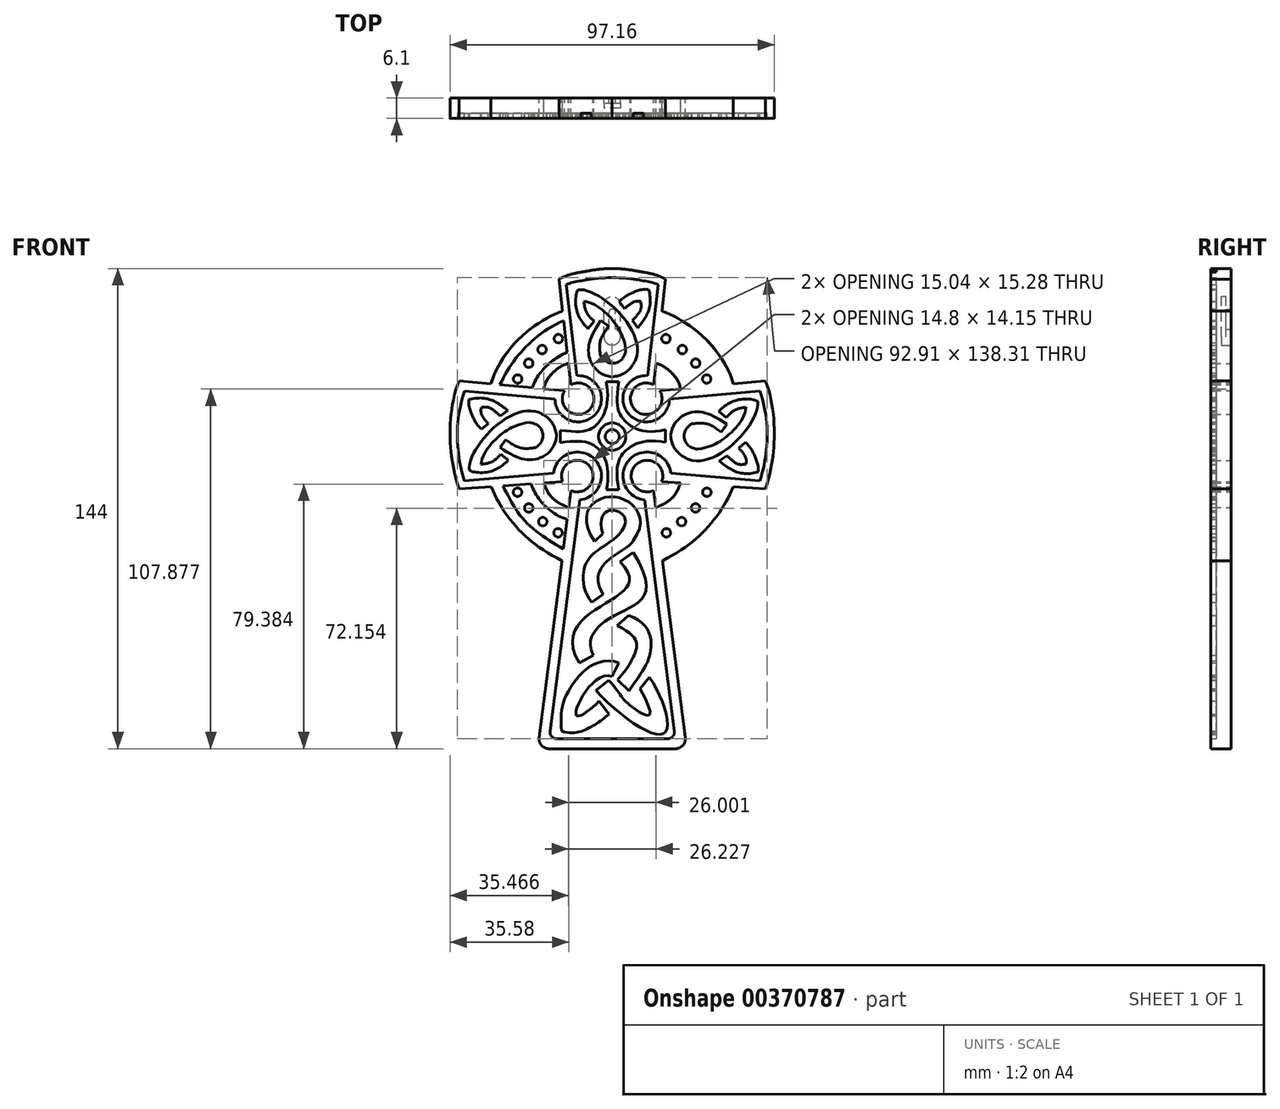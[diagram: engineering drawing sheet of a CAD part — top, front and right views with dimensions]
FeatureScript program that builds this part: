
annotation { "Feature Type Name" : "Feature", "Feature Type Description" : "" }
export const myFeature = defineFeature(function(context is Context, id is Id, definition is map)
    precondition{}
    {
        {
            var Q0;
            Q0=qCreatedBy(makeId("Front.planeOp"),FACE);
            var sketch = newSketch(context, id + "F0", { "sketchPlane" : qUnion([Q0])});
            skLineSegment(sketch, "E0", {"start": v(-15.98, 47.24) * mm, "end": v(-12.37, 15.55) * mm});
            skFitSpline(sketch, "E1", {"points": [v(-15.98, 47.24) * mm, v(-8.08, 49.54) * mm, v(0, 50.37) * mm], "startDerivative": vector(18.02, 9.08) * mm, "endDerivative": vector(16.55, -0.59) * mm});
            skFitSpline(sketch, "E2", {"points": [v(-36.31, 15.75) * mm, v(-28.77, 28.48) * mm, v(-14.9, 37.7) * mm], "startDerivative": vector(4.28, 18.82) * mm, "endDerivative": vector(22.42, 8.54) * mm});
            skLineSegment(sketch, "E3", {"start": v(-45.93, 16.65) * mm, "end": v(-14.25, 13.78) * mm});
            skFitSpline(sketch, "E4", {"points": [v(-45.93, 16.65) * mm, v(-48.57, 0) * mm, v(-45.93, -15.65) * mm], "startDerivative": vector(-12.44, -31.32) * mm, "endDerivative": vector(11.03, -33.67) * mm});
            skLineSegment(sketch, "E5", {"start": v(-45.93, -15.65) * mm, "end": v(-14.86, -13.53) * mm});
            skFitSpline(sketch, "E6", {"points": [v(-20.52, 14.34) * mm, v(-17.86, 19.03) * mm, v(-13.1, 21.9) * mm], "startDerivative": vector(2.95, 13.03) * mm, "endDerivative": vector(12.02, 1.87) * mm});
            skLineSegment(sketch, "E7", {"start": v(-12.37, -16.17) * mm, "end": v(-21.9, -90.24) * mm});
            skFitSpline(sketch, "E8", {"points": [v(-36.23, -14.99) * mm, v(-28.9, -26.9) * mm, v(-15.08, -37.22) * mm], "startDerivative": vector(9.94, -26.4) * mm, "endDerivative": vector(36.07, -18.64) * mm});
            skFitSpline(sketch, "E9", {"points": [v(-20.51, -13.91) * mm, v(-18.02, -18.35) * mm, v(-13.03, -21.31) * mm], "startDerivative": vector(3.98, -10.28) * mm, "endDerivative": vector(10.53, -4.43) * mm});
            skLineSegment(sketch, "E10", {"start": v(-18.92, -93.62) * mm, "end": v(0, -93.62) * mm});
            skArc(sketch, "E11", {"start": v(-14.25, 13.78) * mm, "mid": v(-6.95, 7.9) * mm, "end": v(-12.37, 15.55) * mm});
            skArc(sketch, "E12", {"start": v(-12.37, -16.17) * mm, "mid": v(-6.99, -8.6) * mm, "end": v(-14.86, -13.53) * mm});
            skPoint(sketch, "E13.visualSharp", {"position": v(-22.33, -93.62) * mm});
            skArc(sketch, "E13.filletArc", {"start": v(-21.9, -90.24) * mm, "mid": v(-21.18, -92.6) * mm, "end": v(-18.92, -93.62) * mm});
            skFitSpline(sketch, "E14.MirrorCS", {"points": [v(15.98, 47.24) * mm, v(8.08, 49.54) * mm, v(0, 50.37) * mm], "startDerivative": vector(-18.02, 9.08) * mm, "endDerivative": vector(-16.55, -0.59) * mm});
            skLineSegment(sketch, "E15.MirrorCS", {"start": v(15.98, 47.24) * mm, "end": v(12.37, 15.55) * mm});
            skFitSpline(sketch, "E16.MirrorCS", {"points": [v(36.31, 15.75) * mm, v(28.77, 28.48) * mm, v(14.9, 37.7) * mm], "startDerivative": vector(-4.28, 18.82) * mm, "endDerivative": vector(-22.42, 8.54) * mm});
            skFitSpline(sketch, "E17.MirrorCS", {"points": [v(20.52, 14.34) * mm, v(17.86, 19.03) * mm, v(13.1, 21.9) * mm], "startDerivative": vector(-2.95, 13.03) * mm, "endDerivative": vector(-12.02, 1.87) * mm});
            skLineSegment(sketch, "E18.MirrorCS", {"start": v(45.93, 16.65) * mm, "end": v(14.25, 13.78) * mm});
            skArc(sketch, "E19.MirrorCS", {"start": v(14.25, 13.78) * mm, "mid": v(6.95, 7.9) * mm, "end": v(12.37, 15.55) * mm});
            skFitSpline(sketch, "E20.MirrorCS", {"points": [v(45.93, 16.65) * mm, v(48.57, 0) * mm, v(45.93, -15.65) * mm], "startDerivative": vector(12.44, -31.32) * mm, "endDerivative": vector(-11.03, -33.67) * mm});
            skLineSegment(sketch, "E21.MirrorCS", {"start": v(45.93, -15.65) * mm, "end": v(14.86, -13.53) * mm});
            skArc(sketch, "E22.MirrorCS", {"start": v(12.37, -16.17) * mm, "mid": v(6.99, -8.6) * mm, "end": v(14.86, -13.53) * mm});
            skFitSpline(sketch, "E23.MirrorCS", {"points": [v(20.51, -13.91) * mm, v(18.02, -18.35) * mm, v(13.03, -21.31) * mm], "startDerivative": vector(-3.98, -10.28) * mm, "endDerivative": vector(-10.53, -4.43) * mm});
            skFitSpline(sketch, "E24.MirrorCS", {"points": [v(36.23, -14.99) * mm, v(28.9, -26.9) * mm, v(15.08, -37.22) * mm], "startDerivative": vector(-9.94, -26.4) * mm, "endDerivative": vector(-36.07, -18.64) * mm});
            skLineSegment(sketch, "E25.MirrorCS", {"start": v(12.37, -16.17) * mm, "end": v(21.9, -90.24) * mm});
            skArc(sketch, "E26.MirrorCS", {"start": v(21.9, -90.24) * mm, "mid": v(21.18, -92.6) * mm, "end": v(18.92, -93.62) * mm});
            skLineSegment(sketch, "E27.MirrorCS", {"start": v(18.92, -93.62) * mm, "end": v(0, -93.62) * mm});
            skSolve(sketch);
        }
        {
            var Q0;
            Q0 = qSketchRegion(id + "F0", true);
            extrude(context, id + "F1", {"entities" : qUnion([Q0]), "depth" : 4.5 * mm});
        }
        {
            var Q0;
            Q0=makeQuery(id+"F1.opExtrude","CAP_FACE",FACE,{"disambiguationData":[OSD([sQuery(id+"F0.wireOp",EDGE,"E0"),sQuery(id+"F0.wireOp",EDGE,"E1"),sQuery(id+"F0.wireOp",EDGE,"E2"),sQuery(id+"F0.wireOp",EDGE,"E3"),sQuery(id+"F0.wireOp",EDGE,"E4"),sQuery(id+"F0.wireOp",EDGE,"E5"),sQuery(id+"F0.wireOp",EDGE,"E6"),sQuery(id+"F0.wireOp",EDGE,"E7"),sQuery(id+"F0.wireOp",EDGE,"E8"),sQuery(id+"F0.wireOp",EDGE,"E9"),sQuery(id+"F0.wireOp",EDGE,"E10"),sQuery(id+"F0.wireOp",EDGE,"E11"),sQuery(id+"F0.wireOp",EDGE,"E12"),sQuery(id+"F0.wireOp",EDGE,"E13.filletArc"),sQuery(id+"F0.wireOp",EDGE,"E14.MirrorCS"),sQuery(id+"F0.wireOp",EDGE,"E15.MirrorCS"),sQuery(id+"F0.wireOp",EDGE,"E16.MirrorCS"),sQuery(id+"F0.wireOp",EDGE,"E17.MirrorCS"),sQuery(id+"F0.wireOp",EDGE,"E18.MirrorCS"),sQuery(id+"F0.wireOp",EDGE,"E19.MirrorCS"),sQuery(id+"F0.wireOp",EDGE,"E20.MirrorCS"),sQuery(id+"F0.wireOp",EDGE,"E21.MirrorCS"),sQuery(id+"F0.wireOp",EDGE,"E22.MirrorCS"),sQuery(id+"F0.wireOp",EDGE,"E23.MirrorCS"),sQuery(id+"F0.wireOp",EDGE,"E24.MirrorCS"),sQuery(id+"F0.wireOp",EDGE,"E25.MirrorCS"),sQuery(id+"F0.wireOp",EDGE,"E26.MirrorCS"),sQuery(id+"F0.wireOp",EDGE,"E27.MirrorCS")])],"isStart":false});
            var sketch = newSketch(context, id + "F2", { "sketchPlane" : qUnion([Q0])});
            skLineSegment(sketch, "E28", {"start": v(-15.98, 47.24) * mm, "end": v(-12.37, 15.55) * mm});
            skFitSpline(sketch, "E29", {"points": [v(-13.74, 45.58) * mm, v(-7.87, 46.97) * mm, v(0, 47.69) * mm], "startDerivative": vector(10.43, 4.57) * mm, "endDerivative": vector(27.81, 0.9) * mm});
            skLineSegment(sketch, "E30", {"start": v(-13.74, 45.58) * mm, "end": v(-10.63, 18.29) * mm});
            skLineSegment(sketch, "E31", {"start": v(-45.93, 16.65) * mm, "end": v(-14.25, 13.78) * mm});
            skLineSegment(sketch, "E32", {"start": v(-44.25, 13.64) * mm, "end": v(-17.14, 11.18) * mm});
            skLineSegment(sketch, "E33", {"start": v(-45.93, -15.65) * mm, "end": v(-14.86, -13.53) * mm});
            skLineSegment(sketch, "E34", {"start": v(-44.33, -13.3) * mm, "end": v(-17.59, -11.01) * mm});
            skFitSpline(sketch, "E35", {"points": [v(-44.25, 13.64) * mm, v(-46.45, 0) * mm, v(-44.33, -13.3) * mm], "startDerivative": vector(-9.37, -27.38) * mm, "endDerivative": vector(7.76, -27.9) * mm});
            skFitSpline(sketch, "E36", {"points": [v(-33.66, 15.54) * mm, v(-26.53, 26.22) * mm, v(-14.56, 34.76) * mm], "startDerivative": vector(12.12, 25.5) * mm, "endDerivative": vector(28.6, 12.19) * mm});
            skFitSpline(sketch, "E37", {"points": [v(-23.92, 14.65) * mm, v(-20.1, 20.75) * mm, v(-13.48, 25.31) * mm], "startDerivative": vector(5.37, 16.36) * mm, "endDerivative": vector(16.27, 7.08) * mm});
            skFitSpline(sketch, "E38", {"points": [v(-20.52, 14.34) * mm, v(-17.75, 19.15) * mm, v(-13.1, 21.9) * mm], "startDerivative": vector(3.12, 14.47) * mm, "endDerivative": vector(12.63, 2.18) * mm});
            skLineSegment(sketch, "E39", {"start": v(-12.37, -16.17) * mm, "end": v(-21.9, -90.24) * mm});
            skLineSegment(sketch, "E40", {"start": v(-9.71, -19.02) * mm, "end": v(-18.63, -88.37) * mm});
            skLineSegment(sketch, "E41", {"start": v(-16.65, -90.62) * mm, "end": v(0, -90.62) * mm});
            skLineSegment(sketch, "E42", {"start": v(-18.92, -93.62) * mm, "end": v(0, -93.62) * mm});
            skPoint(sketch, "E43.visualSharp", {"position": v(-22.33, -93.62) * mm});
            skArc(sketch, "E43.filletArc", {"start": v(-21.9, -90.24) * mm, "mid": v(-21.18, -92.6) * mm, "end": v(-18.92, -93.62) * mm});
            skArc(sketch, "E44.filletArc", {"start": v(-18.63, -88.37) * mm, "mid": v(-18.15, -89.94) * mm, "end": v(-16.65, -90.62) * mm});
            skFitSpline(sketch, "E45", {"points": [v(-20.51, -13.91) * mm, v(-17.84, -18.52) * mm, v(-13.03, -21.31) * mm], "startDerivative": vector(4.43, -10.23) * mm, "endDerivative": vector(10.52, -4.59) * mm});
            skFitSpline(sketch, "E46", {"points": [v(-24.29, -14.17) * mm, v(-20.04, -20.86) * mm, v(-13.48, -24.8) * mm], "startDerivative": vector(5.22, -16.41) * mm, "endDerivative": vector(16.74, -4.5) * mm});
            skFitSpline(sketch, "E47", {"points": [v(-32.74, -14.75) * mm, v(-26.14, -25.32) * mm, v(-14.63, -33.74) * mm], "startDerivative": vector(11.58, -23.24) * mm, "endDerivative": vector(24.5, -14.84) * mm});
            skArc(sketch, "E48", {"start": v(-17.14, 11.18) * mm, "mid": v(-5.07, 6.65) * mm, "end": v(-10.63, 18.29) * mm});
            skArc(sketch, "E49", {"start": v(-14.25, 13.78) * mm, "mid": v(-6.95, 7.9) * mm, "end": v(-12.37, 15.55) * mm});
            skArc(sketch, "E50", {"start": v(-9.71, -19.02) * mm, "mid": v(-5.3, -6.8) * mm, "end": v(-17.59, -11.01) * mm});
            skArc(sketch, "E51", {"start": v(-12.37, -16.17) * mm, "mid": v(-6.99, -8.6) * mm, "end": v(-14.86, -13.53) * mm});
            skCircle(sketch, "E52", {"center": v(-16.12, 29.36) * mm, "radius": 1.27 * mm});
            skCircle(sketch, "E53", {"center": v(-21.02, 26.1) * mm, "radius": 1.27 * mm});
            skCircle(sketch, "E54", {"center": v(-25.02, 22) * mm, "radius": 1.27 * mm});
            skCircle(sketch, "E55", {"center": v(-28.32, 17.27) * mm, "radius": 1.27 * mm});
            skCircle(sketch, "E56", {"center": v(-28.36, -16.7) * mm, "radius": 1.27 * mm});
            skCircle(sketch, "E57", {"center": v(-25, -21.4) * mm, "radius": 1.27 * mm});
            skCircle(sketch, "E58", {"center": v(-20.8, -25.52) * mm, "radius": 1.27 * mm});
            skCircle(sketch, "E59", {"center": v(-16.23, -28.86) * mm, "radius": 1.27 * mm});
            skCircle(sketch, "E60.MirrorC", {"center": v(25.02, 22) * mm, "radius": 1.27 * mm});
            skCircle(sketch, "E61.MirrorC", {"center": v(28.32, 17.27) * mm, "radius": 1.27 * mm});
            skFitSpline(sketch, "E62.MirrorCS", {"points": [v(20.51, -13.91) * mm, v(17.84, -18.52) * mm, v(13.03, -21.31) * mm], "startDerivative": vector(-4.43, -10.23) * mm, "endDerivative": vector(-10.52, -4.59) * mm});
            skCircle(sketch, "E63.MirrorC", {"center": v(25, -21.4) * mm, "radius": 1.27 * mm});
            skArc(sketch, "E64.MirrorCS", {"start": v(18.63, -88.37) * mm, "mid": v(18.15, -89.94) * mm, "end": v(16.65, -90.62) * mm});
            skCircle(sketch, "E65.MirrorC", {"center": v(28.36, -16.7) * mm, "radius": 1.27 * mm});
            skCircle(sketch, "E66.MirrorC", {"center": v(21.02, 26.1) * mm, "radius": 1.27 * mm});
            skCircle(sketch, "E67.MirrorC", {"center": v(16.12, 29.36) * mm, "radius": 1.27 * mm});
            skFitSpline(sketch, "E68.MirrorCS", {"points": [v(24.29, -14.17) * mm, v(20.04, -20.86) * mm, v(13.48, -24.8) * mm], "startDerivative": vector(-5.22, -16.41) * mm, "endDerivative": vector(-16.74, -4.5) * mm});
            skCircle(sketch, "E69.MirrorC", {"center": v(16.23, -28.86) * mm, "radius": 1.27 * mm});
            skFitSpline(sketch, "E70.MirrorCS", {"points": [v(23.92, 14.65) * mm, v(20.1, 20.75) * mm, v(13.48, 25.31) * mm], "startDerivative": vector(-5.37, 16.36) * mm, "endDerivative": vector(-16.27, 7.08) * mm});
            skCircle(sketch, "E71.MirrorC", {"center": v(20.8, -25.52) * mm, "radius": 1.27 * mm});
            skFitSpline(sketch, "E72.MirrorCS", {"points": [v(20.52, 14.34) * mm, v(17.75, 19.15) * mm, v(13.1, 21.9) * mm], "startDerivative": vector(-3.12, 14.47) * mm, "endDerivative": vector(-12.63, 2.18) * mm});
            skFitSpline(sketch, "E73.MirrorCS", {"points": [v(13.74, 45.58) * mm, v(7.87, 46.97) * mm, v(0, 47.69) * mm], "startDerivative": vector(-10.43, 4.57) * mm, "endDerivative": vector(-27.81, 0.9) * mm});
            skArc(sketch, "E74.MirrorCS", {"start": v(21.9, -90.24) * mm, "mid": v(21.18, -92.6) * mm, "end": v(18.92, -93.62) * mm});
            skArc(sketch, "E75.MirrorCS", {"start": v(12.37, -16.17) * mm, "mid": v(6.99, -8.6) * mm, "end": v(14.86, -13.53) * mm});
            skArc(sketch, "E76.MirrorCS", {"start": v(17.14, 11.18) * mm, "mid": v(5.07, 6.65) * mm, "end": v(10.63, 18.29) * mm});
            skLineSegment(sketch, "E77.MirrorCS", {"start": v(18.92, -93.62) * mm, "end": v(0, -93.62) * mm});
            skLineSegment(sketch, "E78.MirrorCS", {"start": v(16.65, -90.62) * mm, "end": v(0, -90.62) * mm});
            skFitSpline(sketch, "E79.MirrorCS", {"points": [v(32.74, -14.75) * mm, v(26.14, -25.32) * mm, v(14.63, -33.74) * mm], "startDerivative": vector(-11.58, -23.24) * mm, "endDerivative": vector(-24.5, -14.84) * mm});
            skArc(sketch, "E80.MirrorCS", {"start": v(9.71, -19.02) * mm, "mid": v(5.3, -6.8) * mm, "end": v(17.59, -11.01) * mm});
            skArc(sketch, "E81.MirrorCS", {"start": v(14.25, 13.78) * mm, "mid": v(6.95, 7.9) * mm, "end": v(12.37, 15.55) * mm});
            skFitSpline(sketch, "E82.MirrorCS", {"points": [v(33.66, 15.54) * mm, v(26.53, 26.22) * mm, v(14.56, 34.76) * mm], "startDerivative": vector(-12.12, 25.5) * mm, "endDerivative": vector(-28.6, 12.19) * mm});
            skLineSegment(sketch, "E83.MirrorCS", {"start": v(15.98, 47.24) * mm, "end": v(12.37, 15.55) * mm});
            skLineSegment(sketch, "E84.MirrorCS", {"start": v(13.74, 45.58) * mm, "end": v(10.63, 18.29) * mm});
            skLineSegment(sketch, "E85.MirrorCS", {"start": v(9.71, -19.02) * mm, "end": v(18.63, -88.37) * mm});
            skFitSpline(sketch, "E86.MirrorCS", {"points": [v(44.25, 13.64) * mm, v(46.45, 0) * mm, v(44.33, -13.3) * mm], "startDerivative": vector(9.37, -27.38) * mm, "endDerivative": vector(-7.76, -27.9) * mm});
            skLineSegment(sketch, "E87.MirrorCS", {"start": v(44.33, -13.3) * mm, "end": v(17.59, -11.01) * mm});
            skPoint(sketch, "E88.MirrorP", {"position": v(22.33, -93.62) * mm});
            skLineSegment(sketch, "E89.MirrorCS", {"start": v(12.37, -16.17) * mm, "end": v(21.9, -90.24) * mm});
            skLineSegment(sketch, "E90.MirrorCS", {"start": v(44.25, 13.64) * mm, "end": v(17.14, 11.18) * mm});
            skLineSegment(sketch, "E91.MirrorCS", {"start": v(45.93, -15.65) * mm, "end": v(14.86, -13.53) * mm});
            skLineSegment(sketch, "E92.MirrorCS", {"start": v(45.93, 16.65) * mm, "end": v(14.25, 13.78) * mm});
            skFitSpline(sketch, "E93.0", {"points": [v(-15.98, 47.24) * mm, v(-12.97, 48.76) * mm, v(-8.33, 49.46) * mm, v(-2.75, 50.47) * mm, v(0, 50.37) * mm]});
            skFitSpline(sketch, "E94.0", {"points": [v(-36.31, 15.75) * mm, v(-35.62, 18.8) * mm, v(-29.86, 29.97) * mm, v(-18.74, 36.23) * mm, v(-14.9, 37.7) * mm]});
            skFitSpline(sketch, "E95.0", {"points": [v(-45.93, 16.65) * mm, v(-48.03, 11.35) * mm, v(-49.26, -0.3) * mm, v(-47.74, -10.12) * mm, v(-45.93, -15.65) * mm]});
            skFitSpline(sketch, "E96.0", {"points": [v(-36.23, -14.99) * mm, v(-34.66, -19.16) * mm, v(-29.06, -28.02) * mm, v(-21.4, -33.95) * mm, v(-15.08, -37.22) * mm]});
            skFitSpline(sketch, "E97.MirrorCS", {"points": [v(15.98, 47.24) * mm, v(12.97, 48.76) * mm, v(8.33, 49.46) * mm, v(2.75, 50.47) * mm, v(0, 50.37) * mm]});
            skFitSpline(sketch, "E98.MirrorCS", {"points": [v(36.31, 15.75) * mm, v(35.62, 18.8) * mm, v(29.86, 29.97) * mm, v(18.74, 36.23) * mm, v(14.9, 37.7) * mm]});
            skFitSpline(sketch, "E99.MirrorCS", {"points": [v(45.93, 16.65) * mm, v(48.03, 11.35) * mm, v(49.26, -0.3) * mm, v(47.74, -10.12) * mm, v(45.93, -15.65) * mm]});
            skFitSpline(sketch, "E100.MirrorCS", {"points": [v(36.23, -14.99) * mm, v(34.66, -19.16) * mm, v(29.06, -28.02) * mm, v(21.4, -33.95) * mm, v(15.08, -37.22) * mm]});
            skSolve(sketch);
        }
        {
            var Q0;
            Q0=makeQuery(id+"F2.imprint","IMPRINT",FACE,{"disambiguationData":[TD([[makeQuery(id+"F2.imprint","IMPRINT",EDGE,{"derivedFrom":sQuery(id+"F2.wireOp",EDGE,"E29")}),1.0]])]});
            var Q1;
            {var subQ3=sQuery(id+"F2.wireOp",EDGE,"E36");Q1=makeQuery(id+"F2.imprint","IMPRINT",FACE,{"disambiguationData":[TD([[makeQuery(id+"F2.imprint","IMPRINT",EDGE,{"derivedFrom":subQ3}),1.0]])]});}
            var Q2;
            {var subQ5=sQuery(id+"F2.wireOp",EDGE,"E37");Q2=makeQuery(id+"F2.imprint","IMPRINT",FACE,{"disambiguationData":[TD([[makeQuery(id+"F2.imprint","IMPRINT",EDGE,{"derivedFrom":subQ5}),-1.0]])]});}
            var Q3;
            {var subQ0=sQuery(id+"F2.wireOp",EDGE,"E82.MirrorCS");Q3=makeQuery(id+"F2.imprint","IMPRINT",FACE,{"disambiguationData":[TD([[makeQuery(id+"F2.imprint","IMPRINT",EDGE,{"derivedFrom":subQ0}),-1.0]])]});}
            var Q4;
            {var subQ4=sQuery(id+"F2.wireOp",EDGE,"E68.MirrorCS");Q4=makeQuery(id+"F2.imprint","IMPRINT",FACE,{"disambiguationData":[TD([[makeQuery(id+"F2.imprint","IMPRINT",EDGE,{"derivedFrom":subQ4}),-1.0]])]});}
            var Q5;
            {var subQ0=sQuery(id+"F2.wireOp",EDGE,"E79.MirrorCS");Q5=makeQuery(id+"F2.imprint","IMPRINT",FACE,{"disambiguationData":[TD([[makeQuery(id+"F2.imprint","IMPRINT",EDGE,{"derivedFrom":subQ0}),1.0]])]});}
            var Q6;
            {var subQ0=sQuery(id+"F2.wireOp",EDGE,"E46");Q6=makeQuery(id+"F2.imprint","IMPRINT",FACE,{"disambiguationData":[TD([[makeQuery(id+"F2.imprint","IMPRINT",EDGE,{"derivedFrom":subQ0}),1.0]])]});}
            var Q7;
            {var subQ2=sQuery(id+"F2.wireOp",EDGE,"E47");Q7=makeQuery(id+"F2.imprint","IMPRINT",FACE,{"disambiguationData":[TD([[makeQuery(id+"F2.imprint","IMPRINT",EDGE,{"derivedFrom":subQ2}),-1.0]])]});}
            var Q8;
            Q8=makeQuery(id+"F2.imprint","IMPRINT",FACE,{"disambiguationData":[TD([[makeQuery(id+"F2.imprint","IMPRINT",EDGE,{"derivedFrom":sQuery(id+"F2.wireOp",EDGE,"E56")}),1.0]])]});
            var Q9;
            Q9=makeQuery(id+"F2.imprint","IMPRINT",FACE,{"disambiguationData":[TD([[makeQuery(id+"F2.imprint","IMPRINT",EDGE,{"derivedFrom":sQuery(id+"F2.wireOp",EDGE,"E57")}),1.0]])]});
            var Q10;
            Q10=makeQuery(id+"F2.imprint","IMPRINT",FACE,{"disambiguationData":[TD([[makeQuery(id+"F2.imprint","IMPRINT",EDGE,{"derivedFrom":sQuery(id+"F2.wireOp",EDGE,"E59")}),1.0]])]});
            var Q11;
            Q11=makeQuery(id+"F2.imprint","IMPRINT",FACE,{"disambiguationData":[TD([[makeQuery(id+"F2.imprint","IMPRINT",EDGE,{"derivedFrom":sQuery(id+"F2.wireOp",EDGE,"E58")}),1.0]])]});
            var Q12;
            Q12=makeQuery(id+"F2.imprint","IMPRINT",FACE,{"disambiguationData":[TD([[makeQuery(id+"F2.imprint","IMPRINT",EDGE,{"derivedFrom":sQuery(id+"F2.wireOp",EDGE,"E65.MirrorC")}),-1.0]])]});
            var Q13;
            Q13=makeQuery(id+"F2.imprint","IMPRINT",FACE,{"disambiguationData":[TD([[makeQuery(id+"F2.imprint","IMPRINT",EDGE,{"derivedFrom":sQuery(id+"F2.wireOp",EDGE,"E63.MirrorC")}),-1.0]])]});
            var Q14;
            Q14=makeQuery(id+"F2.imprint","IMPRINT",FACE,{"disambiguationData":[TD([[makeQuery(id+"F2.imprint","IMPRINT",EDGE,{"derivedFrom":sQuery(id+"F2.wireOp",EDGE,"E71.MirrorC")}),-1.0]])]});
            var Q15;
            Q15=makeQuery(id+"F2.imprint","IMPRINT",FACE,{"disambiguationData":[TD([[makeQuery(id+"F2.imprint","IMPRINT",EDGE,{"derivedFrom":sQuery(id+"F2.wireOp",EDGE,"E69.MirrorC")}),-1.0]])]});
            var Q16;
            Q16=makeQuery(id+"F2.imprint","IMPRINT",FACE,{"disambiguationData":[TD([[makeQuery(id+"F2.imprint","IMPRINT",EDGE,{"derivedFrom":sQuery(id+"F2.wireOp",EDGE,"E67.MirrorC")}),-1.0]])]});
            var Q17;
            Q17=makeQuery(id+"F2.imprint","IMPRINT",FACE,{"disambiguationData":[TD([[makeQuery(id+"F2.imprint","IMPRINT",EDGE,{"derivedFrom":sQuery(id+"F2.wireOp",EDGE,"E66.MirrorC")}),-1.0]])]});
            var Q18;
            Q18=makeQuery(id+"F2.imprint","IMPRINT",FACE,{"disambiguationData":[TD([[makeQuery(id+"F2.imprint","IMPRINT",EDGE,{"derivedFrom":sQuery(id+"F2.wireOp",EDGE,"E60.MirrorC")}),-1.0]])]});
            var Q19;
            Q19=makeQuery(id+"F2.imprint","IMPRINT",FACE,{"disambiguationData":[TD([[makeQuery(id+"F2.imprint","IMPRINT",EDGE,{"derivedFrom":sQuery(id+"F2.wireOp",EDGE,"E61.MirrorC")}),-1.0]])]});
            var Q20;
            {var subQ4=sQuery(id+"F2.wireOp",EDGE,"E70.MirrorCS");Q20=makeQuery(id+"F2.imprint","IMPRINT",FACE,{"disambiguationData":[TD([[makeQuery(id+"F2.imprint","IMPRINT",EDGE,{"derivedFrom":subQ4}),1.0]])]});}
            var Q21;
            Q21=makeQuery(id+"F2.imprint","IMPRINT",FACE,{"disambiguationData":[TD([[makeQuery(id+"F2.imprint","IMPRINT",EDGE,{"derivedFrom":sQuery(id+"F2.wireOp",EDGE,"E52")}),1.0]])]});
            var Q22;
            Q22=makeQuery(id+"F2.imprint","IMPRINT",FACE,{"disambiguationData":[TD([[makeQuery(id+"F2.imprint","IMPRINT",EDGE,{"derivedFrom":sQuery(id+"F2.wireOp",EDGE,"E53")}),1.0]])]});
            var Q23;
            Q23=makeQuery(id+"F2.imprint","IMPRINT",FACE,{"disambiguationData":[TD([[makeQuery(id+"F2.imprint","IMPRINT",EDGE,{"derivedFrom":sQuery(id+"F2.wireOp",EDGE,"E54")}),1.0]])]});
            var Q24;
            Q24=makeQuery(id+"F2.imprint","IMPRINT",FACE,{"disambiguationData":[TD([[makeQuery(id+"F2.imprint","IMPRINT",EDGE,{"derivedFrom":sQuery(id+"F2.wireOp",EDGE,"E55")}),1.0]])]});
            extrude(context, id + "F3", {"entities" : qUnion([Q0, Q1, Q2, Q3, Q4, Q5, Q6, Q7, Q8, Q9, Q10, Q11, Q12, Q13, Q14, Q15, Q16, Q17, Q18, Q19, Q20, Q21, Q22, Q23, Q24]), "operationType" : NewBodyOperationType.ADD, "depth" : 1.6 * mm});
        }
        {
            var Q0;
            Q0=makeQuery(id+"F3.boolean.opBoolean","SPLIT",FACE,{"disambiguationData":[TD([makeQuery(id+"F3.opExtrude","SWEPT_FACE",FACE,{"disambiguationData":[OSD([sQuery(id+"F2.wireOp",EDGE,"E29")])]})])],"derivedFrom":makeQuery(id+"F1.opExtrude","CAP_FACE",FACE,{"disambiguationData":[OSD([sQuery(id+"F0.wireOp",EDGE,"E0"),sQuery(id+"F0.wireOp",EDGE,"E1"),sQuery(id+"F0.wireOp",EDGE,"E2"),sQuery(id+"F0.wireOp",EDGE,"E3"),sQuery(id+"F0.wireOp",EDGE,"E4"),sQuery(id+"F0.wireOp",EDGE,"E5"),sQuery(id+"F0.wireOp",EDGE,"E6"),sQuery(id+"F0.wireOp",EDGE,"E7"),sQuery(id+"F0.wireOp",EDGE,"E8"),sQuery(id+"F0.wireOp",EDGE,"E9"),sQuery(id+"F0.wireOp",EDGE,"E10"),sQuery(id+"F0.wireOp",EDGE,"E11"),sQuery(id+"F0.wireOp",EDGE,"E12"),sQuery(id+"F0.wireOp",EDGE,"E13.filletArc"),sQuery(id+"F0.wireOp",EDGE,"E14.MirrorCS"),sQuery(id+"F0.wireOp",EDGE,"E15.MirrorCS"),sQuery(id+"F0.wireOp",EDGE,"E16.MirrorCS"),sQuery(id+"F0.wireOp",EDGE,"E17.MirrorCS"),sQuery(id+"F0.wireOp",EDGE,"E18.MirrorCS"),sQuery(id+"F0.wireOp",EDGE,"E19.MirrorCS"),sQuery(id+"F0.wireOp",EDGE,"E20.MirrorCS"),sQuery(id+"F0.wireOp",EDGE,"E21.MirrorCS"),sQuery(id+"F0.wireOp",EDGE,"E22.MirrorCS"),sQuery(id+"F0.wireOp",EDGE,"E23.MirrorCS"),sQuery(id+"F0.wireOp",EDGE,"E24.MirrorCS"),sQuery(id+"F0.wireOp",EDGE,"E25.MirrorCS"),sQuery(id+"F0.wireOp",EDGE,"E26.MirrorCS"),sQuery(id+"F0.wireOp",EDGE,"E27.MirrorCS")])],"isStart":false})});
            var sketch = newSketch(context, id + "F4", { "sketchPlane" : qUnion([Q0])});
            skFitSpline(sketch, "E101", {"points": [v(-10.27, 44.05) * mm, v(1.63, 37.59) * mm, v(7.12, 23.2) * mm], "startDerivative": vector(19.44, 2.29) * mm, "endDerivative": vector(-9.65, -26.54) * mm});
            skFitSpline(sketch, "E102", {"points": [v(-10.27, 44.05) * mm, v(-10.77, 38.37) * mm, v(-7.27, 32.33) * mm], "startDerivative": vector(-4.28, -6.57) * mm, "endDerivative": vector(10.2, -10.74) * mm});
            skLineSegment(sketch, "E103", {"start": v(-7.27, 32.33) * mm, "end": v(-5.42, 34.64) * mm});
            skFitSpline(sketch, "E104", {"points": [v(-5.42, 34.64) * mm, v(-7.6, 37.04) * mm, v(-8.51, 40.5) * mm], "startDerivative": vector(-5.1, 4.48) * mm, "endDerivative": vector(-1.12, 7.21) * mm});
            skFitSpline(sketch, "E105", {"points": [v(-8.51, 40.5) * mm, v(0, 35.05) * mm, v(4.08, 26.15) * mm], "startDerivative": vector(18.67, -0.82) * mm, "endDerivative": vector(3.63, -23.43) * mm});
            skFitSpline(sketch, "E106", {"points": [v(-3.53, 24.35) * mm, v(0.62, 22) * mm, v(4.08, 26.15) * mm], "startDerivative": vector(5.11, -10.51) * mm, "endDerivative": vector(1.62, 15.64) * mm});
            skFitSpline(sketch, "E107", {"points": [v(-3.44, 34.82) * mm, v(-7, 24.35) * mm, v(0, 17.9) * mm], "startDerivative": vector(-16.54, -24.8) * mm, "endDerivative": vector(26.33, -2.87) * mm});
            skLineSegment(sketch, "E108", {"start": v(-3.44, 34.82) * mm, "end": v(-1.09, 33.12) * mm});
            skFitSpline(sketch, "E109", {"points": [v(-1.09, 33.12) * mm, v(-3.53, 28.74) * mm, v(-3.53, 24.35) * mm], "startDerivative": vector(-5.95, -8.32) * mm, "endDerivative": vector(1.14, -9.21) * mm});
            skFitSpline(sketch, "E110", {"points": [v(0, 17.9) * mm, v(4.68, 19.74) * mm, v(7.12, 23.2) * mm], "startDerivative": vector(11.25, 1.33) * mm, "endDerivative": vector(4.18, 8.1) * mm});
            skFitSpline(sketch, "E111", {"points": [v(2.07, 40.39) * mm, v(5.9, 43.03) * mm, v(10.9, 44.16) * mm], "startDerivative": vector(9.87, 10.5) * mm, "endDerivative": vector(13.91, -0.9) * mm});
            skLineSegment(sketch, "E112", {"start": v(2.07, 40.39) * mm, "end": v(3.72, 38.32) * mm});
            skFitSpline(sketch, "E113", {"points": [v(3.72, 38.32) * mm, v(5.84, 40.03) * mm, v(8.58, 40.44) * mm], "startDerivative": vector(3.96, 4.08) * mm, "endDerivative": vector(7.1, -2.16) * mm});
            skFitSpline(sketch, "E114", {"points": [v(8.58, 40.44) * mm, v(8.11, 37.29) * mm, v(6.05, 34.8) * mm], "startDerivative": vector(1.51, -10.58) * mm, "endDerivative": vector(-4.27, -4.3) * mm});
            skLineSegment(sketch, "E115", {"start": v(6.05, 34.8) * mm, "end": v(7.65, 32.53) * mm});
            skFitSpline(sketch, "E116", {"points": [v(10.9, 44.16) * mm, v(10.9, 37.75) * mm, v(7.65, 32.53) * mm], "startDerivative": vector(4, -14.43) * mm, "endDerivative": vector(-8.2, -10.02) * mm});
            skFitSpline(sketch, "E117", {"points": [v(43.63, 10.56) * mm, v(37.18, -1.34) * mm, v(22.79, -6.83) * mm], "startDerivative": vector(2.29, -19.44) * mm, "endDerivative": vector(-26.54, 9.65) * mm});
            skFitSpline(sketch, "E118", {"points": [v(43.63, 10.56) * mm, v(37.96, 11.06) * mm, v(31.92, 7.56) * mm], "startDerivative": vector(-6.57, 4.28) * mm, "endDerivative": vector(-10.74, -10.2) * mm});
            skLineSegment(sketch, "E119", {"start": v(31.92, 7.56) * mm, "end": v(34.23, 5.72) * mm});
            skFitSpline(sketch, "E120", {"points": [v(34.23, 5.72) * mm, v(36.62, 7.88) * mm, v(40.08, 8.8) * mm], "startDerivative": vector(4.48, 5.1) * mm, "endDerivative": vector(7.21, 1.12) * mm});
            skFitSpline(sketch, "E121", {"points": [v(40.08, 8.8) * mm, v(34.64, 0.3) * mm, v(25.74, -3.78) * mm], "startDerivative": vector(-0.82, -18.67) * mm, "endDerivative": vector(-23.43, -3.63) * mm});
            skFitSpline(sketch, "E122", {"points": [v(23.94, 3.82) * mm, v(21.59, -0.33) * mm, v(25.74, -3.78) * mm], "startDerivative": vector(-10.51, -5.11) * mm, "endDerivative": vector(15.64, -1.62) * mm});
            skFitSpline(sketch, "E123", {"points": [v(34.4, 3.73) * mm, v(23.94, 7.28) * mm, v(17.49, 0.3) * mm], "startDerivative": vector(-24.8, 16.54) * mm, "endDerivative": vector(-2.87, -26.33) * mm});
            skLineSegment(sketch, "E124", {"start": v(34.4, 3.73) * mm, "end": v(32.7, 1.38) * mm});
            skFitSpline(sketch, "E125", {"points": [v(32.7, 1.38) * mm, v(28.32, 3.82) * mm, v(23.94, 3.82) * mm], "startDerivative": vector(-8.32, 5.95) * mm, "endDerivative": vector(-9.21, -1.14) * mm});
            skFitSpline(sketch, "E126", {"points": [v(17.49, 0.3) * mm, v(19.33, -4.38) * mm, v(22.79, -6.83) * mm], "startDerivative": vector(1.33, -11.25) * mm, "endDerivative": vector(8.1, -4.18) * mm});
            skFitSpline(sketch, "E127", {"points": [v(39.98, -1.77) * mm, v(42.61, -5.6) * mm, v(43.75, -10.61) * mm], "startDerivative": vector(10.5, -9.87) * mm, "endDerivative": vector(-0.9, -13.91) * mm});
            skLineSegment(sketch, "E128", {"start": v(39.98, -1.77) * mm, "end": v(37.9, -3.43) * mm});
            skFitSpline(sketch, "E129", {"points": [v(37.9, -3.43) * mm, v(39.61, -5.55) * mm, v(40.03, -8.29) * mm], "startDerivative": vector(4.08, -3.96) * mm, "endDerivative": vector(-2.16, -7.1) * mm});
            skFitSpline(sketch, "E130", {"points": [v(40.03, -8.29) * mm, v(36.87, -7.82) * mm, v(34.4, -5.75) * mm], "startDerivative": vector(-10.58, -1.51) * mm, "endDerivative": vector(-4.3, 4.27) * mm});
            skLineSegment(sketch, "E131", {"start": v(34.4, -5.75) * mm, "end": v(32.12, -7.36) * mm});
            skFitSpline(sketch, "E132", {"points": [v(43.75, -10.61) * mm, v(37.34, -10.61) * mm, v(32.12, -7.36) * mm], "startDerivative": vector(-14.43, -4) * mm, "endDerivative": vector(-10.02, 8.2) * mm});
            skFitSpline(sketch, "E133", {"points": [v(-42.83, -10.1) * mm, v(-36.37, 1.8) * mm, v(-21.99, 7.28) * mm], "startDerivative": vector(-2.29, 19.44) * mm, "endDerivative": vector(26.54, -9.65) * mm});
            skFitSpline(sketch, "E134", {"points": [v(-42.83, -10.1) * mm, v(-37.16, -10.6) * mm, v(-31.12, -7.1) * mm], "startDerivative": vector(6.57, -4.28) * mm, "endDerivative": vector(10.74, 10.2) * mm});
            skLineSegment(sketch, "E135", {"start": v(-31.12, -7.1) * mm, "end": v(-33.42, -5.26) * mm});
            skFitSpline(sketch, "E136", {"points": [v(-33.42, -5.26) * mm, v(-35.82, -7.43) * mm, v(-39.28, -8.35) * mm], "startDerivative": vector(-4.48, -5.1) * mm, "endDerivative": vector(-7.21, -1.12) * mm});
            skFitSpline(sketch, "E137", {"points": [v(-39.28, -8.35) * mm, v(-33.84, 0.16) * mm, v(-24.94, 4.24) * mm], "startDerivative": vector(0.82, 18.67) * mm, "endDerivative": vector(23.43, 3.63) * mm});
            skFitSpline(sketch, "E138", {"points": [v(-23.14, -3.37) * mm, v(-20.79, 0.78) * mm, v(-24.94, 4.24) * mm], "startDerivative": vector(10.51, 5.11) * mm, "endDerivative": vector(-15.64, 1.62) * mm});
            skFitSpline(sketch, "E139", {"points": [v(-33.6, -3.28) * mm, v(-23.14, -6.83) * mm, v(-16.68, 0.16) * mm], "startDerivative": vector(24.8, -16.54) * mm, "endDerivative": vector(2.87, 26.33) * mm});
            skLineSegment(sketch, "E140", {"start": v(-33.6, -3.28) * mm, "end": v(-31.9, -0.93) * mm});
            skFitSpline(sketch, "E141", {"points": [v(-31.9, -0.93) * mm, v(-27.52, -3.37) * mm, v(-23.14, -3.37) * mm], "startDerivative": vector(8.32, -5.95) * mm, "endDerivative": vector(9.21, 1.14) * mm});
            skFitSpline(sketch, "E142", {"points": [v(-16.68, 0.16) * mm, v(-18.53, 4.84) * mm, v(-21.99, 7.28) * mm], "startDerivative": vector(-1.33, 11.25) * mm, "endDerivative": vector(-8.1, 4.18) * mm});
            skFitSpline(sketch, "E143", {"points": [v(-39.17, 2.23) * mm, v(-41.8, 6.05) * mm, v(-42.95, 11.07) * mm], "startDerivative": vector(-10.5, 9.87) * mm, "endDerivative": vector(0.9, 13.91) * mm});
            skLineSegment(sketch, "E144", {"start": v(-39.17, 2.23) * mm, "end": v(-37.1, 3.88) * mm});
            skFitSpline(sketch, "E145", {"points": [v(-37.1, 3.88) * mm, v(-38.81, 6) * mm, v(-39.23, 8.74) * mm], "startDerivative": vector(-4.08, 3.96) * mm, "endDerivative": vector(2.16, 7.1) * mm});
            skFitSpline(sketch, "E146", {"points": [v(-39.23, 8.74) * mm, v(-36.07, 8.28) * mm, v(-33.6, 6.2) * mm], "startDerivative": vector(10.58, 1.51) * mm, "endDerivative": vector(4.3, -4.27) * mm});
            skLineSegment(sketch, "E147", {"start": v(-33.6, 6.2) * mm, "end": v(-31.32, 7.81) * mm});
            skFitSpline(sketch, "E148", {"points": [v(-42.95, 11.07) * mm, v(-36.54, 11.07) * mm, v(-31.32, 7.81) * mm], "startDerivative": vector(14.43, 4) * mm, "endDerivative": vector(10.02, -8.2) * mm});
            skLineSegment(sketch, "E149", {"start": v(-1.8, 16.45) * mm, "end": v(1.94, 16.45) * mm});
            skLineSegment(sketch, "E150", {"start": v(-15.51, 1.88) * mm, "end": v(-15.51, -1.87) * mm});
            skLineSegment(sketch, "E151", {"start": v(16, 2.07) * mm, "end": v(16, -1.68) * mm});
            skLineSegment(sketch, "E152", {"start": v(-1.74, -15.93) * mm, "end": v(2.01, -15.93) * mm});
            skFitSpline(sketch, "E153", {"points": [v(-15.51, 1.88) * mm, v(-4.1, 4.16) * mm, v(-1.8, 16.45) * mm], "startDerivative": vector(41.53, -6) * mm, "endDerivative": vector(-7.24, 33.18) * mm});
            skFitSpline(sketch, "E154", {"points": [v(-15.51, -1.87) * mm, v(-3.97, -3.85) * mm, v(-1.74, -15.93) * mm], "startDerivative": vector(36.43, 6.33) * mm, "endDerivative": vector(-6.89, -32.53) * mm});
            skFitSpline(sketch, "E155", {"points": [v(1.94, 16.45) * mm, v(3.98, 4.53) * mm, v(16, 2.07) * mm], "startDerivative": vector(-6.7, -43.47) * mm, "endDerivative": vector(38.32, 9.21) * mm});
            skFitSpline(sketch, "E156", {"points": [v(2.01, -15.93) * mm, v(3.92, -4.34) * mm, v(16, -1.68) * mm], "startDerivative": vector(-8.24, 38.97) * mm, "endDerivative": vector(36.87, -6.51) * mm});
            skCircle(sketch, "E157", {"center": v(0, 0) * mm, "radius": 4.09 * mm});
            skCircle(sketch, "E158", {"center": v(0, 0) * mm, "radius": 2.1 * mm});
            skFitSpline(sketch, "E159", {"points": [v(-5.27, -31.46) * mm, v(0, -18.05) * mm, v(6.33, -31.13) * mm], "startDerivative": vector(-34.58, 49.25) * mm, "endDerivative": vector(-32.37, -42.28) * mm});
            skLineSegment(sketch, "E160", {"start": v(-5.27, -31.46) * mm, "end": v(-2.89, -29.18) * mm});
            skLineSegment(sketch, "E161", {"start": v(-6.14, -49.78) * mm, "end": v(-2.74, -47.25) * mm});
            skLineSegment(sketch, "E162", {"start": v(2.4, -37.58) * mm, "end": v(6.33, -34.7) * mm});
            skLineSegment(sketch, "E163", {"start": v(-9.88, -67.91) * mm, "end": v(-5.61, -65.64) * mm});
            skLineSegment(sketch, "E164", {"start": v(1.46, -56.65) * mm, "end": v(4.94, -53.62) * mm});
            skLineSegment(sketch, "E165", {"start": v(0, -71.9) * mm, "end": v(1.98, -67.85) * mm});
            skLineSegment(sketch, "E166", {"start": v(1.57, -72.93) * mm, "end": v(5.1, -76.25) * mm});
            skLineSegment(sketch, "E167", {"start": v(8.3, -75.62) * mm, "end": v(11.1, -72.2) * mm});
            skLineSegment(sketch, "E168", {"start": v(-4.86, -76.14) * mm, "end": v(-1.03, -73.03) * mm});
            skLineSegment(sketch, "E169", {"start": v(-3.93, -79.36) * mm, "end": v(-0.92, -83.2) * mm});
            skFitSpline(sketch, "E170", {"points": [v(-2.74, -47.25) * mm, v(-0.92, -36.85) * mm, v(6.33, -31.13) * mm], "startDerivative": vector(-17.76, 26.07) * mm, "endDerivative": vector(5.76, 12.4) * mm});
            skPoint(sketch, "E171.2.internal.snap0", {"position": v(-4.08, -30.32) * mm});
            skFitSpline(sketch, "E171", {"points": [v(-2.89, -29.18) * mm, v(1.67, -22.45) * mm, v(1.05, -30.32) * mm], "startDerivative": vector(-9.9, 40.84) * mm, "endDerivative": vector(-27, -25.74) * mm});
            skFitSpline(sketch, "E172", {"points": [v(-6.14, -49.78) * mm, v(-7.35, -37.17) * mm, v(1.05, -30.32) * mm], "startDerivative": vector(-19.57, 26.74) * mm, "endDerivative": vector(22.66, 18.13) * mm});
            skFitSpline(sketch, "E173", {"points": [v(2.4, -37.58) * mm, v(0, -48.78) * mm, v(-9.88, -67.91) * mm], "startDerivative": vector(37.41, -39.45) * mm, "endDerivative": vector(32.56, -54.63) * mm});
            skFitSpline(sketch, "E174", {"points": [v(-5.61, -65.64) * mm, v(1.88, -53.03) * mm, v(6.33, -34.7) * mm], "startDerivative": vector(-20.4, 36.98) * mm, "endDerivative": vector(-46.26, 76.55) * mm});
            skFitSpline(sketch, "E175", {"points": [v(1.98, -67.85) * mm, v(-12.64, -75.52) * mm, v(-15.12, -88.27) * mm], "startDerivative": vector(-36.97, 13.5) * mm, "endDerivative": vector(3.97, -31.1) * mm});
            skFitSpline(sketch, "E176", {"points": [v(4.94, -53.62) * mm, v(11.52, -64.43) * mm, v(5.1, -76.25) * mm], "startDerivative": vector(40.1, -13.46) * mm, "endDerivative": vector(-23.9, -35.53) * mm});
            skFitSpline(sketch, "E177", {"points": [v(1.46, -56.65) * mm, v(7.06, -64.22) * mm, v(1.57, -72.93) * mm], "startDerivative": vector(37.54, -18.45) * mm, "endDerivative": vector(-16.42, -17.43) * mm});
            skFitSpline(sketch, "E178", {"points": [v(-1.03, -73.03) * mm, v(6.33, -81.33) * mm, v(8.3, -75.62) * mm], "startDerivative": vector(20, -22.7) * mm, "endDerivative": vector(-46.15, 80.59) * mm});
            skFitSpline(sketch, "E179", {"points": [v(-4.86, -76.14) * mm, v(15.66, -88.9) * mm, v(11.1, -72.2) * mm], "startDerivative": vector(38.47, -42.49) * mm, "endDerivative": vector(-26.46, 37.32) * mm});
            skFitSpline(sketch, "E180", {"points": [v(0, -71.9) * mm, v(-10.87, -83.3) * mm, v(-3.93, -79.36) * mm], "startDerivative": vector(-28.16, 9.05) * mm, "endDerivative": vector(22.43, 21.69) * mm});
            skFitSpline(sketch, "E181", {"points": [v(-15.12, -88.27) * mm, v(-7.04, -87.44) * mm, v(-0.92, -83.2) * mm], "startDerivative": vector(18.26, -6.7) * mm, "endDerivative": vector(11.7, 10.42) * mm});
            skSolve(sketch);
        }
        {
            var Q0;
            Q0 = qSketchRegion(id + "F4", true);
            var Q1;
            Q1=makeQuery(id+"F4.imprint","IMPRINT",FACE,{"disambiguationData":[TD([[makeQuery(id+"F4.imprint","IMPRINT",EDGE,{"derivedFrom":sQuery(id+"F4.wireOp",EDGE,"E158")}),1.0]])]});
            extrude(context, id + "F5", {"entities" : qUnion([Q0, Q1]), "operationType" : NewBodyOperationType.ADD, "depth" : 1.6 * mm});
        }
        {
            var Q0;
            Q0=makeQuery(id+"F1.opExtrude","CAP_FACE",FACE,{"disambiguationData":[OSD([sQuery(id+"F0.wireOp",EDGE,"E0"),sQuery(id+"F0.wireOp",EDGE,"E1"),sQuery(id+"F0.wireOp",EDGE,"E2"),sQuery(id+"F0.wireOp",EDGE,"E3"),sQuery(id+"F0.wireOp",EDGE,"E4"),sQuery(id+"F0.wireOp",EDGE,"E5"),sQuery(id+"F0.wireOp",EDGE,"E6"),sQuery(id+"F0.wireOp",EDGE,"E7"),sQuery(id+"F0.wireOp",EDGE,"E8"),sQuery(id+"F0.wireOp",EDGE,"E9"),sQuery(id+"F0.wireOp",EDGE,"E10"),sQuery(id+"F0.wireOp",EDGE,"E11"),sQuery(id+"F0.wireOp",EDGE,"E12"),sQuery(id+"F0.wireOp",EDGE,"E13.filletArc"),sQuery(id+"F0.wireOp",EDGE,"E14.MirrorCS"),sQuery(id+"F0.wireOp",EDGE,"E15.MirrorCS"),sQuery(id+"F0.wireOp",EDGE,"E16.MirrorCS"),sQuery(id+"F0.wireOp",EDGE,"E17.MirrorCS"),sQuery(id+"F0.wireOp",EDGE,"E18.MirrorCS"),sQuery(id+"F0.wireOp",EDGE,"E19.MirrorCS"),sQuery(id+"F0.wireOp",EDGE,"E20.MirrorCS"),sQuery(id+"F0.wireOp",EDGE,"E21.MirrorCS"),sQuery(id+"F0.wireOp",EDGE,"E22.MirrorCS"),sQuery(id+"F0.wireOp",EDGE,"E23.MirrorCS"),sQuery(id+"F0.wireOp",EDGE,"E24.MirrorCS"),sQuery(id+"F0.wireOp",EDGE,"E25.MirrorCS"),sQuery(id+"F0.wireOp",EDGE,"E26.MirrorCS"),sQuery(id+"F0.wireOp",EDGE,"E27.MirrorCS")])],"isStart":true});
            var sketch = newSketch(context, id + "F6", { "sketchPlane" : qUnion([Q0])});
            skCircle(sketch, "E182", {"center": v(0, 29.93) * mm, "radius": 2.5 * mm});
            skLineSegment(sketch, "E183", {"start": v(-1, 32.22) * mm, "end": v(-1, 37.22) * mm});
            skLineSegment(sketch, "E184", {"start": v(1, 32.22) * mm, "end": v(1, 37.22) * mm});
            skArc(sketch, "E185", {"start": v(-1, 37.22) * mm, "mid": v(0, 38.22) * mm, "end": v(1, 37.22) * mm});
            skSolve(sketch);
        }
        {
            var Q0;
            {var subQ0=sQuery(id+"F6.wireOp",EDGE,"E182");var subQ1=makeQuery(id+"F6.imprint","INTERSECT",VERTEX,{"derivedFrom":[subQ0,sQuery(id+"F6.wireOp",EDGE,"E184")]});Q0=makeQuery(id+"F6.imprint","IMPRINT",FACE,{"disambiguationData":[TD([[makeQuery(id+"F6.imprint","IMPRINT",EDGE,{"disambiguationData":[TD([[subQ1,1.0]])],"derivedFrom":subQ0}),1.0]])]});}
            var Q1;
            {var subQ0=sQuery(id+"F6.wireOp",EDGE,"E183");Q1=makeQuery(id+"F6.imprint","IMPRINT",FACE,{"disambiguationData":[TD([[makeQuery(id+"F6.imprint","IMPRINT",EDGE,{"derivedFrom":subQ0}),-1.0]])]});}
            extrude(context, id + "F7", {"entities" : qUnion([Q0, Q1]), "operationType" : NewBodyOperationType.REMOVE, "oppositeDirection" : true, "depth" : 3 * mm});
        }
        {
            var Q0;
            Q0=makeQuery(id+"F1.opExtrude","CAP_FACE",FACE,{"disambiguationData":[OSD([sQuery(id+"F0.wireOp",EDGE,"E0"),sQuery(id+"F0.wireOp",EDGE,"E1"),sQuery(id+"F0.wireOp",EDGE,"E2"),sQuery(id+"F0.wireOp",EDGE,"E3"),sQuery(id+"F0.wireOp",EDGE,"E4"),sQuery(id+"F0.wireOp",EDGE,"E5"),sQuery(id+"F0.wireOp",EDGE,"E6"),sQuery(id+"F0.wireOp",EDGE,"E7"),sQuery(id+"F0.wireOp",EDGE,"E8"),sQuery(id+"F0.wireOp",EDGE,"E9"),sQuery(id+"F0.wireOp",EDGE,"E10"),sQuery(id+"F0.wireOp",EDGE,"E11"),sQuery(id+"F0.wireOp",EDGE,"E12"),sQuery(id+"F0.wireOp",EDGE,"E13.filletArc"),sQuery(id+"F0.wireOp",EDGE,"E14.MirrorCS"),sQuery(id+"F0.wireOp",EDGE,"E15.MirrorCS"),sQuery(id+"F0.wireOp",EDGE,"E16.MirrorCS"),sQuery(id+"F0.wireOp",EDGE,"E17.MirrorCS"),sQuery(id+"F0.wireOp",EDGE,"E18.MirrorCS"),sQuery(id+"F0.wireOp",EDGE,"E19.MirrorCS"),sQuery(id+"F0.wireOp",EDGE,"E20.MirrorCS"),sQuery(id+"F0.wireOp",EDGE,"E21.MirrorCS"),sQuery(id+"F0.wireOp",EDGE,"E22.MirrorCS"),sQuery(id+"F0.wireOp",EDGE,"E23.MirrorCS"),sQuery(id+"F0.wireOp",EDGE,"E24.MirrorCS"),sQuery(id+"F0.wireOp",EDGE,"E25.MirrorCS"),sQuery(id+"F0.wireOp",EDGE,"E26.MirrorCS"),sQuery(id+"F0.wireOp",EDGE,"E27.MirrorCS")])],"isStart":true});
            cPlane(context, id + "F8", {"entities" : qUnion([Q0]), "cplaneType" : CPlaneType.OFFSET, "offset" : 3 * mm, "oppositeDirection" : true, "width" : 150 * mm, "height" : 150 * mm});
        }
        {
            var Q0;
            Q0=qCreatedBy(id+"F8.planeOp",FACE);
            var sketch = newSketch(context, id + "F9", { "sketchPlane" : qUnion([Q0])});
            skArc(sketch, "E186.0", {"start": v(-2.5, 39.43) * mm, "mid": v(0, 41.93) * mm, "end": v(2.5, 39.43) * mm});
            skLineSegment(sketch, "E187.0", {"start": v(-2.5, 29.93) * mm, "end": v(-2.5, 39.43) * mm});
            skLineSegment(sketch, "E188.0", {"start": v(2.5, 29.93) * mm, "end": v(2.5, 39.43) * mm});
            skLineSegment(sketch, "E189.0", {"start": v(-1, 32.22) * mm, "end": v(-1, 37.22) * mm});
            skArc(sketch, "E189.1", {"start": v(-1, 37.22) * mm, "mid": v(0, 38.22) * mm, "end": v(1, 37.22) * mm});
            skLineSegment(sketch, "E189.2", {"start": v(1, 32.22) * mm, "end": v(1, 37.22) * mm});
            skArc(sketch, "E190.0", {"start": v(-1, 32.22) * mm, "mid": v(-2.1, 31.3) * mm, "end": v(-2.5, 29.93) * mm});
            skArc(sketch, "E191.trimOffspring", {"start": v(2.5, 29.93) * mm, "mid": v(2.1, 31.3) * mm, "end": v(1, 32.22) * mm});
            skSolve(sketch);
        }
        {
            var Q0;
            Q0 = qSketchRegion(id + "F9", true);
            extrude(context, id + "F10", {"entities" : qUnion([Q0]), "operationType" : NewBodyOperationType.REMOVE, "depth" : 1.5 * mm});
        }
    });
